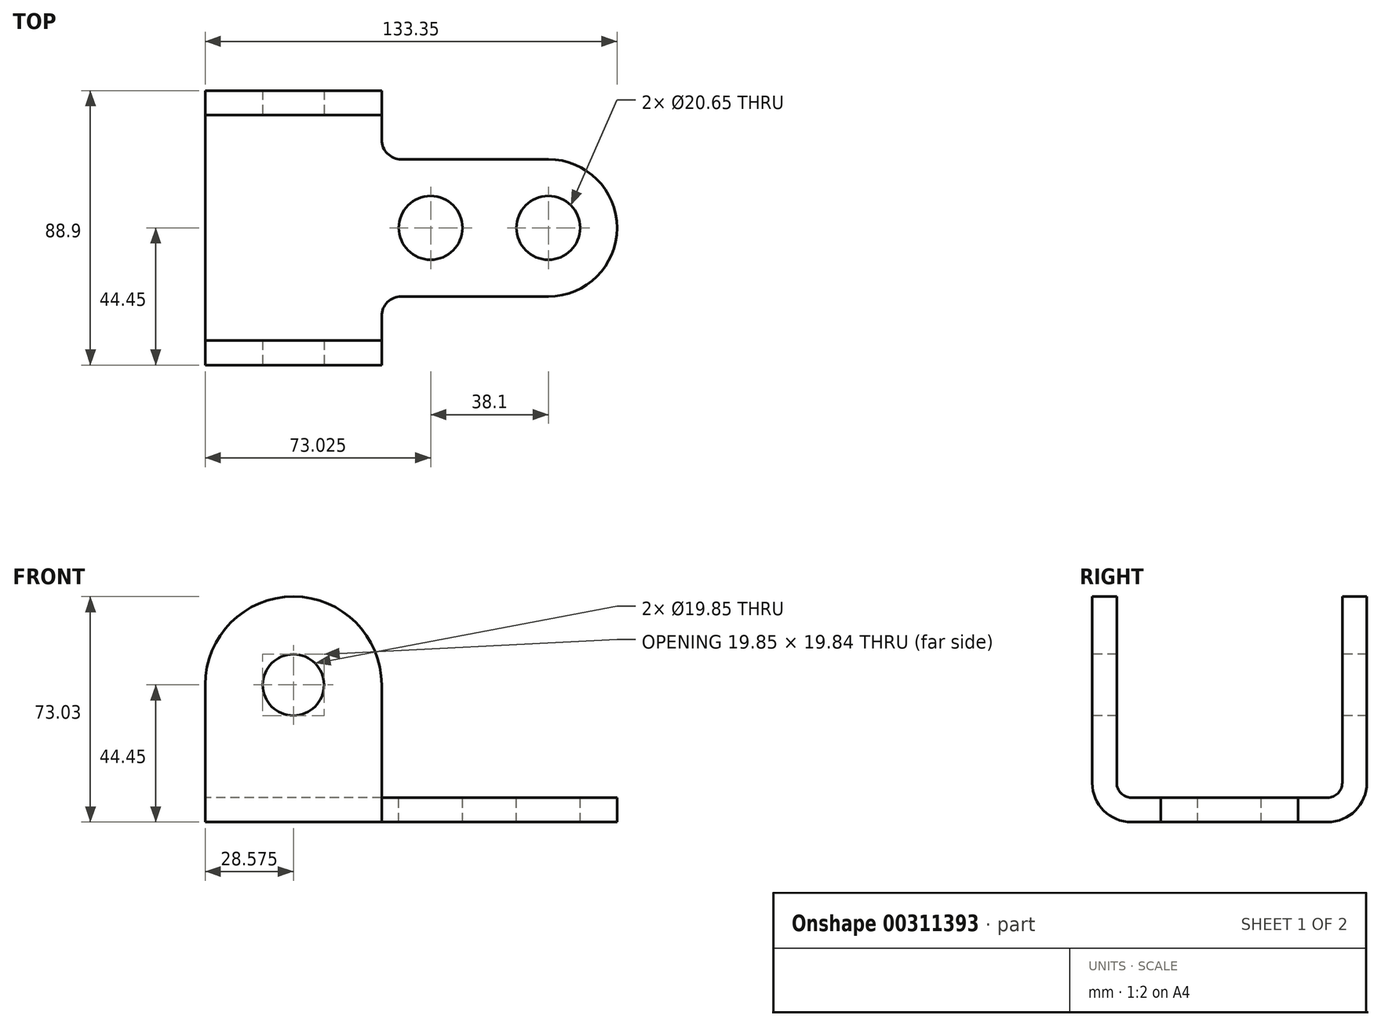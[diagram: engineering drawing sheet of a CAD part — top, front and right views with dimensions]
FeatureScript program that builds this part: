
annotation { "Feature Type Name" : "Feature", "Feature Type Description" : "" }
export const myFeature = defineFeature(function(context is Context, id is Id, definition is map)
    precondition{}
    {
        {
            var Q0;
            Q0=qCreatedBy(makeId("Right.planeOp"),FACE);
            var sketch = newSketch(context, id + "F0", { "sketchPlane" : qUnion([Q0])});
            skLineSegment(sketch, "E0", {"start": v(44.45, 73.03) * mm, "end": v(44.45, 0) * mm});
            skLineSegment(sketch, "E1", {"start": v(44.45, 0) * mm, "end": v(-44.45, 0) * mm});
            skLineSegment(sketch, "E2", {"start": v(-44.45, 0) * mm, "end": v(-44.45, 73.03) * mm});
            skLineSegment(sketch, "E3", {"start": v(-44.45, 73.03) * mm, "end": v(-36.51, 73.03) * mm});
            skLineSegment(sketch, "E4", {"start": v(-36.51, 73.03) * mm, "end": v(-36.51, 7.94) * mm});
            skLineSegment(sketch, "E5", {"start": v(-36.51, 7.94) * mm, "end": v(36.51, 7.94) * mm});
            skLineSegment(sketch, "E6", {"start": v(36.51, 7.94) * mm, "end": v(36.51, 73.03) * mm});
            skLineSegment(sketch, "E7", {"start": v(36.51, 73.03) * mm, "end": v(44.45, 73.03) * mm});
            skSolve(sketch);
        }
        {
            var Q0;
            Q0=makeQuery(id+"F0.imprint","IMPRINT",FACE,{"disambiguationData":[TD([[makeQuery(id+"F0.imprint","IMPRINT",EDGE,{"derivedFrom":sQuery(id+"F0.wireOp",EDGE,"E0")}),-1.0]])]});
            extrude(context, id + "F1", {"entities" : qUnion([Q0]), "depth" : 133.35 * mm});
        }
        {
            var Q0;
            Q0=makeQuery(id+"F1.opExtrude","SWEPT_FACE",FACE,{"disambiguationData":[OSD([sQuery(id+"F0.wireOp",EDGE,"E2")])]});
            var sketch = newSketch(context, id + "F2", { "sketchPlane" : qUnion([Q0])});
            skArc(sketch, "E8", {"start": v(57.15, 44.45) * mm, "mid": v(28.58, 73.03) * mm, "end": v(0, 44.45) * mm});
            skLineSegment(sketch, "E9", {"start": v(57.15, 44.45) * mm, "end": v(57.15, 7.94) * mm});
            skLineSegment(sketch, "E10", {"start": v(0, 44.45) * mm, "end": v(0, 0) * mm});
            skLineSegment(sketch, "E11", {"start": v(0, 0) * mm, "end": v(57.15, 0) * mm});
            skLineSegment(sketch, "E12", {"start": v(57.15, 7.94) * mm, "end": v(133.35, 7.94) * mm});
            skLineSegment(sketch, "E13", {"start": v(133.35, 7.94) * mm, "end": v(133.35, 0) * mm});
            skLineSegment(sketch, "E14", {"start": v(133.35, 0) * mm, "end": v(0, 0) * mm});
            skSolve(sketch);
        }
        {
            var Q0;
            {var subQ0=sQuery(id+"F2.wireOp",EDGE,"E8");var subQ1=sQuery(id+"F0.wireOp",EDGE,"E2");var subQ2=makeQuery(id+"F1.opExtrude","CAP_EDGE",EDGE,{"disambiguationData":[OSD([subQ1])],"isStart":true});var subQ3=makeQuery(id+"F2.imprint","INTERSECT",VERTEX,{"derivedFrom":[subQ2,subQ0,sQuery(id+"F2.wireOp",EDGE,"E10")]});Q0=makeQuery(id+"F2.imprint","IMPRINT",FACE,{"disambiguationData":[TD([[makeQuery(id+"F2.imprint","IMPRINT",EDGE,{"disambiguationData":[TD([[subQ3,1.0]])],"derivedFrom":subQ0}),-1.0]])]});}
            var Q1;
            {var subQ5=sQuery(id+"F2.wireOp",EDGE,"E9");Q1=makeQuery(id+"F2.imprint","IMPRINT",FACE,{"disambiguationData":[TD([[makeQuery(id+"F2.imprint","IMPRINT",EDGE,{"derivedFrom":subQ5}),1.0]])]});}
            extrude(context, id + "F3", {"entities" : qUnion([Q0, Q1]), "operationType" : NewBodyOperationType.REMOVE, "endBound" : BoundingType.THROUGH_ALL, "oppositeDirection" : true, "depth" : 25.4 * mm});
        }
        {
            var Q0;
            Q0=makeQuery(id+"F1.opExtrude","SWEPT_FACE",FACE,{"disambiguationData":[OSD([sQuery(id+"F0.wireOp",EDGE,"E2")])]});
            var sketch = newSketch(context, id + "F4", { "sketchPlane" : qUnion([Q0])});
            skCircle(sketch, "E15", {"center": v(28.58, 44.45) * mm, "radius": 9.92 * mm});
            skSolve(sketch);
        }
        {
            var Q0;
            Q0 = qSketchRegion(id + "F4", true);
            extrude(context, id + "F5", {"entities" : qUnion([Q0]), "operationType" : NewBodyOperationType.REMOVE, "endBound" : BoundingType.THROUGH_ALL, "oppositeDirection" : true, "depth" : 25.4 * mm});
        }
        {
            var Q0;
            Q0=makeQuery(id+"F3.boolean.opBoolean","MERGE",FACE,{"derivedFrom":[makeQuery(id+"F1.opExtrude","SWEPT_FACE",FACE,{"disambiguationData":[OSD([sQuery(id+"F0.wireOp",EDGE,"E5")])]}),makeQuery(id+"F3.opExtrude","SWEPT_FACE",FACE,{"disambiguationData":[OSD([sQuery(id+"F2.wireOp",EDGE,"E12")])]})]});
            var sketch = newSketch(context, id + "F6", { "sketchPlane" : qUnion([Q0])});
            skArc(sketch, "E16", {"start": v(111.13, -22.22) * mm, "mid": v(133.35, 0) * mm, "end": v(111.13, 22.23) * mm});
            skCircle(sketch, "E17", {"center": v(111.13, 0) * mm, "radius": 10.33 * mm});
            skCircle(sketch, "E18", {"center": v(73.03, 0) * mm, "radius": 10.33 * mm});
            skLineSegment(sketch, "E19", {"start": v(57.15, 44.45) * mm, "end": v(57.15, 28.57) * mm});
            skLineSegment(sketch, "E20", {"start": v(111.13, 22.22) * mm, "end": v(63.5, 22.22) * mm});
            skLineSegment(sketch, "E21", {"start": v(111.13, -22.23) * mm, "end": v(63.5, -22.23) * mm});
            skLineSegment(sketch, "E22.trimOffspring", {"start": v(57.15, -28.58) * mm, "end": v(57.15, -44.45) * mm});
            skPoint(sketch, "E23.visualSharp", {"position": v(57.15, 22.22) * mm});
            skArc(sketch, "E23.filletArc", {"start": v(57.15, 28.57) * mm, "mid": v(59, 24.08) * mm, "end": v(63.5, 22.22) * mm});
            skPoint(sketch, "E24.visualSharp", {"position": v(57.15, -22.23) * mm});
            skArc(sketch, "E24.filletArc", {"start": v(63.5, -22.23) * mm, "mid": v(59, -24.08) * mm, "end": v(57.15, -28.58) * mm});
            skSolve(sketch);
        }
        {
            var Q0;
            Q0=makeQuery(id+"F6.imprint","IMPRINT",FACE,{"disambiguationData":[TD([[makeQuery(id+"F6.imprint","IMPRINT",EDGE,{"derivedFrom":sQuery(id+"F6.wireOp",EDGE,"E18")}),1.0]])]});
            var Q1;
            Q1=makeQuery(id+"F6.imprint","IMPRINT",FACE,{"disambiguationData":[TD([[makeQuery(id+"F6.imprint","IMPRINT",EDGE,{"derivedFrom":sQuery(id+"F6.wireOp",EDGE,"E17")}),1.0]])]});
            var Q2;
            {var subQ6=sQuery(id+"F6.wireOp",EDGE,"E20");Q2=makeQuery(id+"F6.imprint","IMPRINT",FACE,{"disambiguationData":[TD([[makeQuery(id+"F6.imprint","IMPRINT",EDGE,{"derivedFrom":subQ6}),-1.0]])]});}
            var Q3;
            {var subQ6=sQuery(id+"F6.wireOp",EDGE,"E21");Q3=makeQuery(id+"F6.imprint","IMPRINT",FACE,{"disambiguationData":[TD([[makeQuery(id+"F6.imprint","IMPRINT",EDGE,{"derivedFrom":subQ6}),1.0]])]});}
            extrude(context, id + "F7", {"entities" : qUnion([Q0, Q1, Q2, Q3]), "operationType" : NewBodyOperationType.REMOVE, "oppositeDirection" : true, "depth" : 25.4 * mm});
        }
        {
            var Q0;
            Q0=makeQuery(id+"F1.opExtrude","SWEPT_EDGE",EDGE,{"disambiguationData":[OSD([sQuery(id+"F0.wireOp",EDGE,"E5"),sQuery(id+"F0.wireOp",EDGE,"E6")])]});
            var Q1;
            Q1=makeQuery(id+"F1.opExtrude","SWEPT_EDGE",EDGE,{"disambiguationData":[OSD([sQuery(id+"F0.wireOp",EDGE,"E4"),sQuery(id+"F0.wireOp",EDGE,"E5")])]});
            fillet(context, id + "F8", {"entities" : qUnion([Q0, Q1]), "radius" : 4.76 * mm, "tangentPropagation" : true, "allowEdgeOverflow" : false});
        }
        {
            var Q0;
            Q0=makeQuery(id+"F1.opExtrude","SWEPT_EDGE",EDGE,{"disambiguationData":[OSD([sQuery(id+"F0.wireOp",EDGE,"E1"),sQuery(id+"F0.wireOp",EDGE,"E2")])]});
            var Q1;
            Q1=makeQuery(id+"F1.opExtrude","SWEPT_EDGE",EDGE,{"disambiguationData":[OSD([sQuery(id+"F0.wireOp",EDGE,"E0"),sQuery(id+"F0.wireOp",EDGE,"E1")])]});
            fillet(context, id + "F9", {"entities" : qUnion([Q0, Q1]), "radius" : 12.7 * mm, "tangentPropagation" : true, "allowEdgeOverflow" : false});
        }
    });
